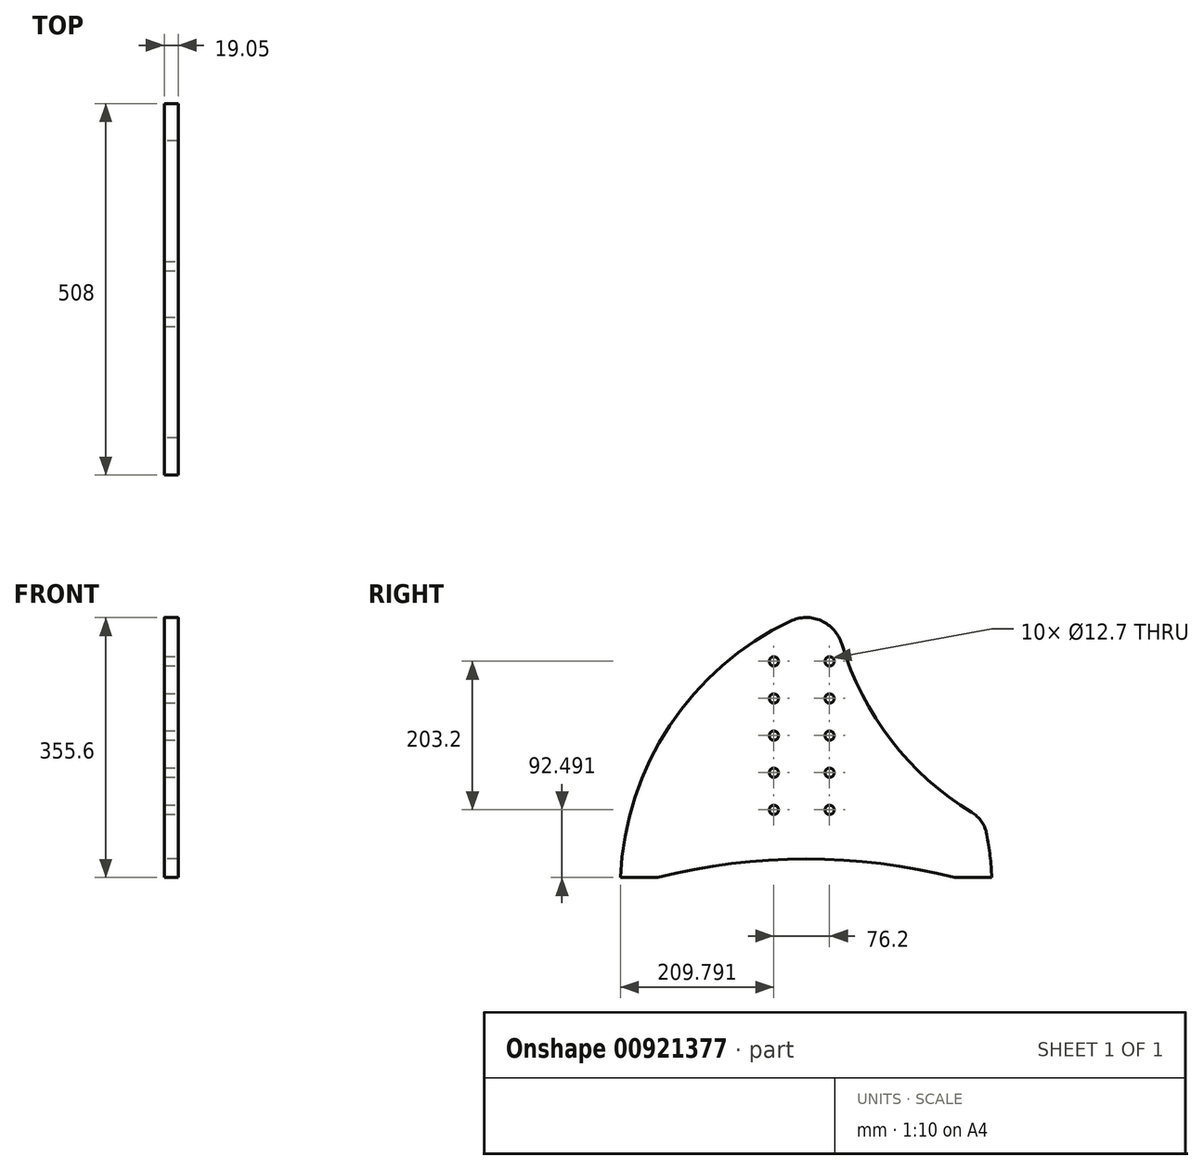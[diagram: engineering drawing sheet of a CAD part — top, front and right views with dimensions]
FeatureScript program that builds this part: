
annotation { "Feature Type Name" : "Feature", "Feature Type Description" : "" }
export const myFeature = defineFeature(function(context is Context, id is Id, definition is map)
    precondition{}
    {
        {
            var Q0;
            Q0=qCreatedBy(makeId("Right.planeOp"),FACE);
            var sketch = newSketch(context, id + "F0", { "sketchPlane" : qUnion([Q0])});
            skLineSegment(sketch, "E0.bottom", {"start": v(-254, 177.8) * mm, "end": v(254, 177.8) * mm, "construction": true});
            skLineSegment(sketch, "E0.left", {"start": v(-254, 177.8) * mm, "end": v(-254, -177.8) * mm, "construction": true});
            skLineSegment(sketch, "E0.right", {"start": v(254, 177.8) * mm, "end": v(254, -177.8) * mm, "construction": true});
            skLineSegment(sketch, "E1", {"start": v(-254, 177.8) * mm, "end": v(254, -177.8) * mm, "construction": true});
            skLineSegment(sketch, "E2", {"start": v(-254, -177.8) * mm, "end": v(-203.2, -177.8) * mm});
            skLineSegment(sketch, "E3", {"start": v(254, -177.8) * mm, "end": v(203.2, -177.8) * mm});
            skLineSegment(sketch, "E4", {"start": v(-254, -152.4) * mm, "end": v(254, -152.4) * mm, "construction": true});
            skArc(sketch, "E5", {"start": v(203.2, -177.8) * mm, "mid": v(0, -152.4) * mm, "end": v(-203.2, -177.8) * mm});
            skLineSegment(sketch, "E6", {"start": v(-203.2, -177.8) * mm, "end": v(203.2, -177.8) * mm, "construction": true});
            skLineSegment(sketch, "E7", {"start": v(0, 177.8) * mm, "end": v(0, -264.82) * mm, "construction": true});
            skPoint(sketch, "E7.endSnap0", {"position": v(0, -177.8) * mm});
            skArc(sketch, "E8", {"start": v(48.66, 141.6) * mm, "mid": v(20.66, 173.4) * mm, "end": v(-21.72, 172.92) * mm});
            skArc(sketch, "E9", {"start": v(-21.72, 172.92) * mm, "mid": v(-186.77, 29.95) * mm, "end": v(-254, -177.8) * mm});
            skArc(sketch, "E10", {"start": v(48.66, 141.6) * mm, "mid": v(116.26, 9.96) * mm, "end": v(226.5, -88.74) * mm});
            skArc(sketch, "E11.MirrorCS", {"start": v(247.2, -118.64) * mm, "mid": v(251.69, -148.1) * mm, "end": v(254, -177.8) * mm});
            skPoint(sketch, "E12.orphan", {"position": v(21.72, 172.92) * mm});
            skPoint(sketch, "E13.center.orphan", {"position": v(203.2, -127) * mm});
            skArc(sketch, "E14.trimOffspring", {"start": v(247.2, -118.64) * mm, "mid": v(240.03, -101.5) * mm, "end": v(226.5, -88.74) * mm});
            skSolve(sketch);
        }
        {
            var Q0;
            Q0 = qSketchRegion(id + "F0", true);
            extrude(context, id + "F1", {"entities" : qUnion([Q0]), "depth" : 19.05 * mm, "offsetDistance" : 25.4 * mm});
        }
        {
            var Q0;
            Q0=makeQuery(id+"F1.opExtrude","CAP_FACE",FACE,{"disambiguationData":[OSD([sQuery(id+"F0.wireOp",EDGE,"E2"),sQuery(id+"F0.wireOp",EDGE,"E3"),sQuery(id+"F0.wireOp",EDGE,"E5"),sQuery(id+"F0.wireOp",EDGE,"E8"),sQuery(id+"F0.wireOp",EDGE,"E9"),sQuery(id+"F0.wireOp",EDGE,"E10"),sQuery(id+"F0.wireOp",EDGE,"E11.MirrorCS"),sQuery(id+"F0.wireOp",EDGE,"E14.trimOffspring")])],"isStart":false});
            var sketch = newSketch(context, id + "F2", { "sketchPlane" : qUnion([Q0])});
            skCircle(sketch, "E15", {"center": v(32, -85.3) * mm, "radius": 6.35 * mm});
            skCircle(sketch, "E16.0.1.0", {"center": v(32, -34.5) * mm, "radius": 6.35 * mm});
            skCircle(sketch, "E16.0.2.0", {"center": v(32, 16.3) * mm, "radius": 6.35 * mm});
            skCircle(sketch, "E16.0.3.0", {"center": v(32, 67.1) * mm, "radius": 6.35 * mm});
            skCircle(sketch, "E16.1.0.0", {"center": v(-44.2, -85.3) * mm, "radius": 6.35 * mm});
            skCircle(sketch, "E16.1.1.0", {"center": v(-44.2, -34.5) * mm, "radius": 6.35 * mm});
            skCircle(sketch, "E16.1.2.0", {"center": v(-44.2, 16.3) * mm, "radius": 6.35 * mm});
            skCircle(sketch, "E16.1.3.0", {"center": v(-44.2, 67.1) * mm, "radius": 6.35 * mm});
            skLineSegment(sketch, "E16.direction1", {"start": v(32, -85.3) * mm, "end": v(-44.2, -85.3) * mm, "construction": true});
            skLineSegment(sketch, "E16.direction2", {"start": v(32, -85.3) * mm, "end": v(32, -34.5) * mm, "construction": true});
            skCircle(sketch, "E17.0.0.4", {"center": v(32, 117.9) * mm, "radius": 6.35 * mm});
            skCircle(sketch, "E17.0.1.4", {"center": v(-44.2, 117.9) * mm, "radius": 6.35 * mm});
            skLineSegment(sketch, "E18", {"start": v(32, -85.3) * mm, "end": v(-44.2, 117.9) * mm, "construction": true});
            skSolve(sketch);
        }
        {
            var Q0;
            Q0 = qSketchRegion(id + "F2", true);
            extrude(context, id + "F3", {"entities" : qUnion([Q0]), "operationType" : NewBodyOperationType.REMOVE, "endBound" : BoundingType.THROUGH_ALL, "oppositeDirection" : true, "depth" : 25.4 * mm, "offsetDistance" : 25.4 * mm});
        }
    });
